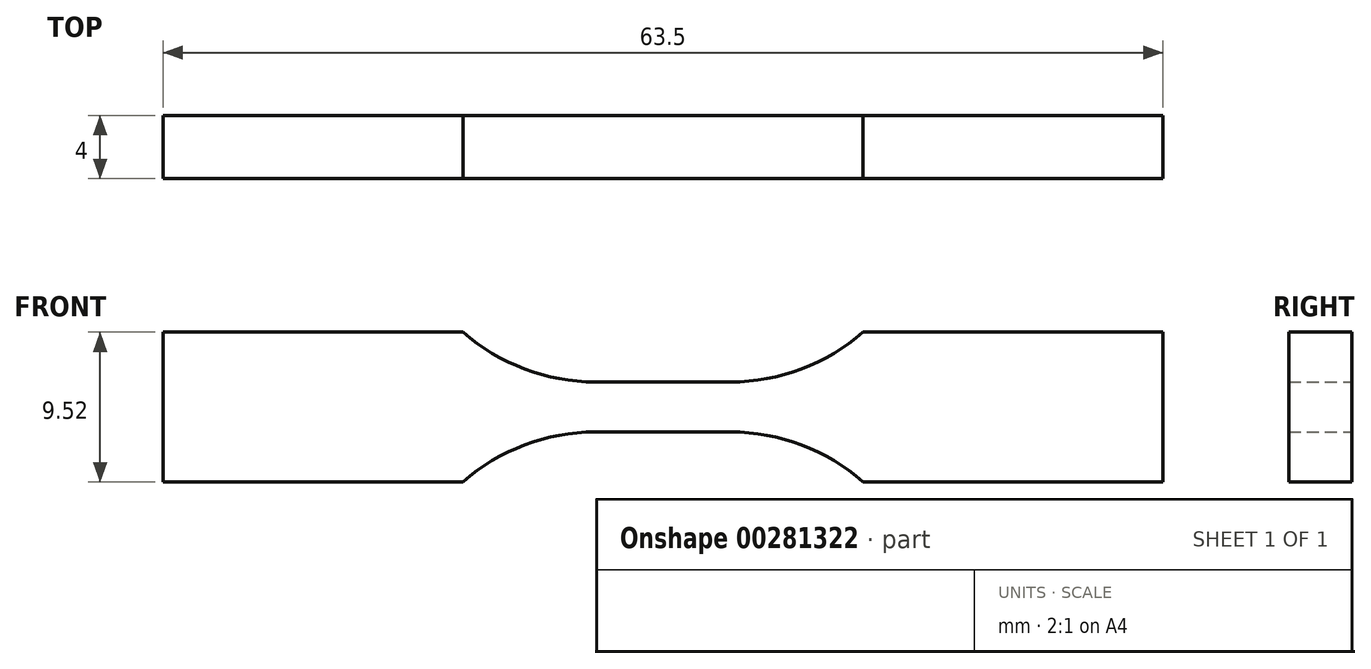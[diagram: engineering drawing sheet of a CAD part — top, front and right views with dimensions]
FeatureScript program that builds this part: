
annotation { "Feature Type Name" : "Feature", "Feature Type Description" : "" }
export const myFeature = defineFeature(function(context is Context, id is Id, definition is map)
    precondition{}
    {
        {
            var Q0;
            Q0=qCreatedBy(makeId("Front.planeOp"),FACE);
            var sketch = newSketch(context, id + "F0", { "sketchPlane" : qUnion([Q0])});
            skLineSegment(sketch, "E0", {"start": v(0, 1.59) * mm, "end": v(4.3, 1.59) * mm});
            skArc(sketch, "E1", {"start": v(4.3, 1.59) * mm, "mid": v(8.79, 2.4) * mm, "end": v(12.7, 4.76) * mm});
            skLineSegment(sketch, "E2", {"start": v(12.7, 4.76) * mm, "end": v(31.75, 4.76) * mm});
            skLineSegment(sketch, "E3", {"start": v(31.75, 4.76) * mm, "end": v(31.75, 0) * mm});
            skLineSegment(sketch, "E4.MirrorCS", {"start": v(0, -1.59) * mm, "end": v(4.3, -1.59) * mm});
            skLineSegment(sketch, "E5.MirrorCS", {"start": v(31.75, -4.76) * mm, "end": v(31.75, 0) * mm});
            skLineSegment(sketch, "E6.MirrorCS", {"start": v(12.7, -4.76) * mm, "end": v(31.75, -4.76) * mm});
            skArc(sketch, "E7.MirrorCS", {"start": v(4.3, -1.59) * mm, "mid": v(8.79, -2.4) * mm, "end": v(12.7, -4.76) * mm});
            skArc(sketch, "E8.MirrorCS", {"start": v(-4.3, -1.59) * mm, "mid": v(-8.79, -2.4) * mm, "end": v(-12.7, -4.76) * mm});
            skLineSegment(sketch, "E9.MirrorCS", {"start": v(-12.7, -4.76) * mm, "end": v(-31.75, -4.76) * mm});
            skArc(sketch, "E10.MirrorCS", {"start": v(-4.3, 1.59) * mm, "mid": v(-8.79, 2.4) * mm, "end": v(-12.7, 4.76) * mm});
            skLineSegment(sketch, "E11.MirrorCS", {"start": v(-12.7, 4.76) * mm, "end": v(-31.75, 4.76) * mm});
            skLineSegment(sketch, "E12.MirrorCS", {"start": v(-31.75, -4.76) * mm, "end": v(-31.75, 0) * mm});
            skLineSegment(sketch, "E13.MirrorCS", {"start": v(0, -1.59) * mm, "end": v(-4.3, -1.59) * mm});
            skLineSegment(sketch, "E14.MirrorCS", {"start": v(-31.75, 4.76) * mm, "end": v(-31.75, 0) * mm});
            skLineSegment(sketch, "E15.MirrorCS", {"start": v(0, 1.59) * mm, "end": v(-4.3, 1.59) * mm});
            skSolve(sketch);
        }
        {
            var Q0;
            Q0 = qSketchRegion(id + "F0", true);
            extrude(context, id + "F1", {"entities" : qUnion([Q0]), "endBound" : BoundingType.SYMMETRIC, "depth" : 4 * mm});
        }
    });
